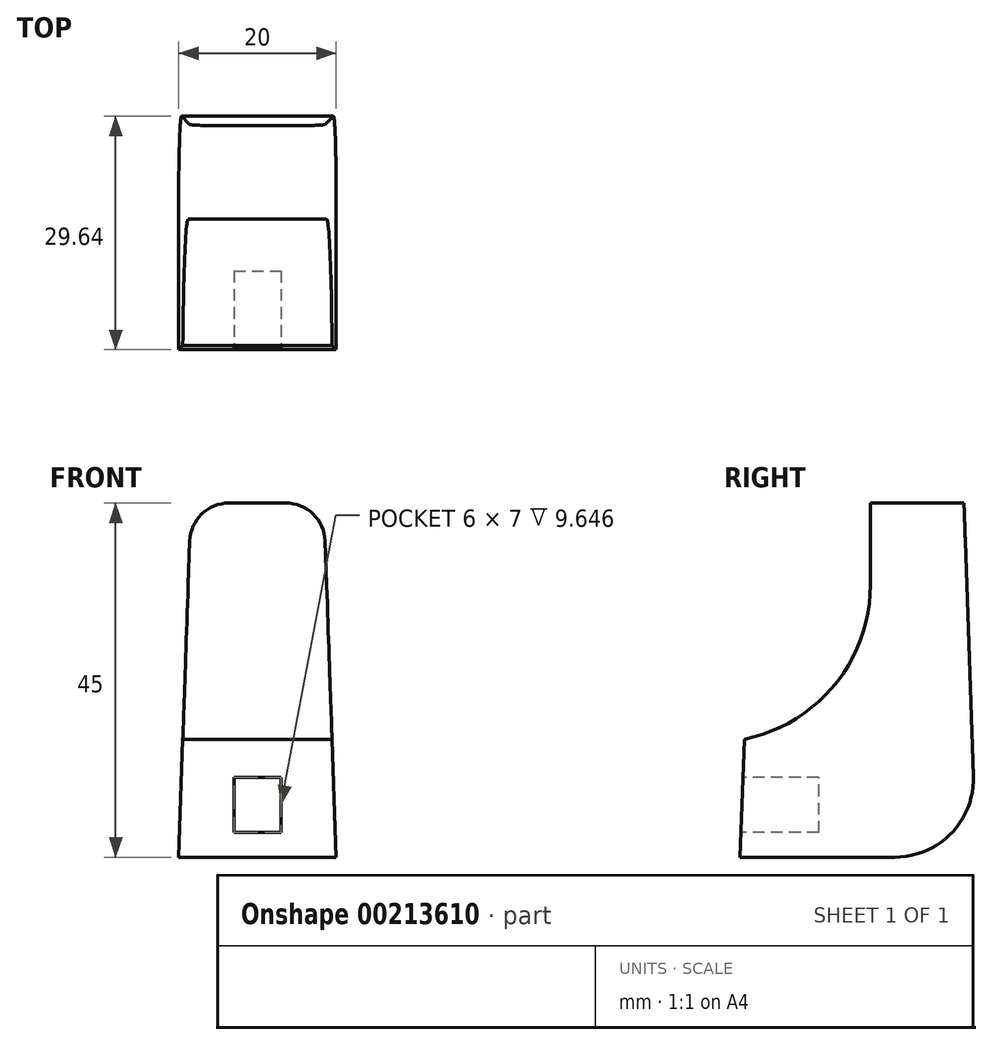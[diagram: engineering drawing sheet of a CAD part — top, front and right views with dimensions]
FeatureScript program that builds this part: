
annotation { "Feature Type Name" : "Feature", "Feature Type Description" : "" }
export const myFeature = defineFeature(function(context is Context, id is Id, definition is map)
    precondition{}
    {
        {
            var Q0;
            Q0=qCreatedBy(makeId("Top.planeOp"),FACE);
            var sketch = newSketch(context, id + "F0", { "sketchPlane" : qUnion([Q0])});
            skLineSegment(sketch, "E0.bottom", {"start": v(-10, -15) * mm, "end": v(10, -15) * mm});
            skLineSegment(sketch, "E0.top", {"start": v(-10, 15) * mm, "end": v(10, 15) * mm});
            skLineSegment(sketch, "E0.left", {"start": v(-10, -15) * mm, "end": v(-10, 15) * mm});
            skLineSegment(sketch, "E0.right", {"start": v(10, -15) * mm, "end": v(10, 15) * mm});
            skPoint(sketch, "E0.middle", {"position": v(0, 0) * mm});
            skSolve(sketch);
        }
        {
            var Q0;
            Q0 = qSketchRegion(id + "F0", true);
            extrude(context, id + "F1", {"entities" : qUnion([Q0]), "depth" : 45 * mm, "hasDraft" : true, "draftAngle" : 2 * degree, "draftPullDirection" : true});
        }
        {
            var Q0;
            Q0=qCreatedBy(makeId("Right.planeOp"),FACE);
            var Q1;
            Q1=makeQuery(id+"F1.opExtrude","CAP_EDGE",EDGE,{"disambiguationData":[OSD([sQuery(id+"F0.wireOp",EDGE,"E0.left")])],"isStart":true});
            cPlane(context, id + "F2", {"entities" : qUnion([Q0, Q1]), "cplaneType" : CPlaneType.LINE_ANGLE, "offset" : 25 * mm, "angle" : 0 * degree, "width" : 150 * mm, "height" : 150 * mm});
        }
        {
            var Q0;
            Q0=qCreatedBy(id+"F2.planeOp",FACE);
            var sketch = newSketch(context, id + "F3", { "sketchPlane" : qUnion([Q0])});
            skLineSegment(sketch, "E1.bottom", {"start": v(13.43, 45) * mm, "end": v(-1.57, 45) * mm});
            skLineSegment(sketch, "E1.top", {"start": v(13.43, 15) * mm, "end": v(-1.57, 15) * mm});
            skLineSegment(sketch, "E1.right", {"start": v(-1.57, 45) * mm, "end": v(-1.57, 15) * mm});
            skLineSegment(sketch, "E2", {"start": v(13.43, 15) * mm, "end": v(14.48, 15) * mm});
            skLineSegment(sketch, "E3", {"start": v(13.43, 45) * mm, "end": v(14.48, 15) * mm});
            skSolve(sketch);
        }
        {
            var Q0;
            Q0 = qSketchRegion(id + "F3", true);
            extrude(context, id + "F4", {"entities" : qUnion([Q0]), "operationType" : NewBodyOperationType.REMOVE, "endBound" : BoundingType.THROUGH_ALL, "oppositeDirection" : true, "depth" : 25 * mm});
        }
        {
            var Q0;
            Q0=makeQuery(id+"F4.boolean.opBoolean","COPY",EDGE,{"derivedFrom":makeQuery(id+"F4.opExtrude","SWEPT_EDGE",EDGE,{"disambiguationData":[OSD([sQuery(id+"F3.wireOp",EDGE,"E1.top"),sQuery(id+"F3.wireOp",EDGE,"E1.right")])]})});
            fillet(context, id + "F5", {"entities" : qUnion([Q0]), "radius" : 20 * mm, "tangentPropagation" : true, "allowEdgeOverflow" : false});
        }
        {
            var Q0;
            Q0=qCreatedBy(makeId("Front.planeOp"),FACE);
            var Q1;
            Q1=makeQuery(id+"F1.opExtrude","CAP_EDGE",EDGE,{"disambiguationData":[OSD([sQuery(id+"F0.wireOp",EDGE,"E0.bottom")])],"isStart":true});
            cPlane(context, id + "F6", {"entities" : qUnion([Q0, Q1]), "cplaneType" : CPlaneType.LINE_ANGLE, "offset" : 25 * mm, "angle" : 0 * degree, "width" : 150 * mm, "height" : 150 * mm});
        }
        {
            var Q0;
            Q0=qCreatedBy(id+"F6.planeOp",FACE);
            var sketch = newSketch(context, id + "F7", { "sketchPlane" : qUnion([Q0])});
            skLineSegment(sketch, "E4.bottom", {"start": v(3, 3.13) * mm, "end": v(-3, 3.13) * mm});
            skLineSegment(sketch, "E4.top", {"start": v(3, 10.13) * mm, "end": v(-3, 10.13) * mm});
            skLineSegment(sketch, "E4.left", {"start": v(3, 3.13) * mm, "end": v(3, 10.13) * mm});
            skLineSegment(sketch, "E4.right", {"start": v(-3, 3.13) * mm, "end": v(-3, 10.13) * mm});
            skPoint(sketch, "E4.middle", {"position": v(0, 6.63) * mm});
            skSolve(sketch);
        }
        {
            var Q0;
            Q0 = qSketchRegion(id + "F7", true);
            extrude(context, id + "F8", {"entities" : qUnion([Q0]), "operationType" : NewBodyOperationType.REMOVE, "depth" : 10 * mm});
        }
        {
            var Q0;
            Q0=makeQuery(id+"F1.opExtrude","CAP_EDGE",EDGE,{"disambiguationData":[OSD([sQuery(id+"F0.wireOp",EDGE,"E0.left")])],"isStart":false});
            var Q1;
            Q1=makeQuery(id+"F1.opExtrude","CAP_EDGE",EDGE,{"disambiguationData":[OSD([sQuery(id+"F0.wireOp",EDGE,"E0.right")])],"isStart":false});
            fillet(context, id + "F9", {"entities" : qUnion([Q0, Q1]), "radius" : 5 * mm, "tangentPropagation" : true, "allowEdgeOverflow" : false});
        }
        {
            var Q0;
            Q0=makeQuery(id+"F1.opExtrude","CAP_EDGE",EDGE,{"disambiguationData":[OSD([sQuery(id+"F0.wireOp",EDGE,"E0.top")])],"isStart":true});
            fillet(context, id + "F10", {"entities" : qUnion([Q0]), "radius" : 10 * mm, "tangentPropagation" : true, "allowEdgeOverflow" : false});
        }
    });
